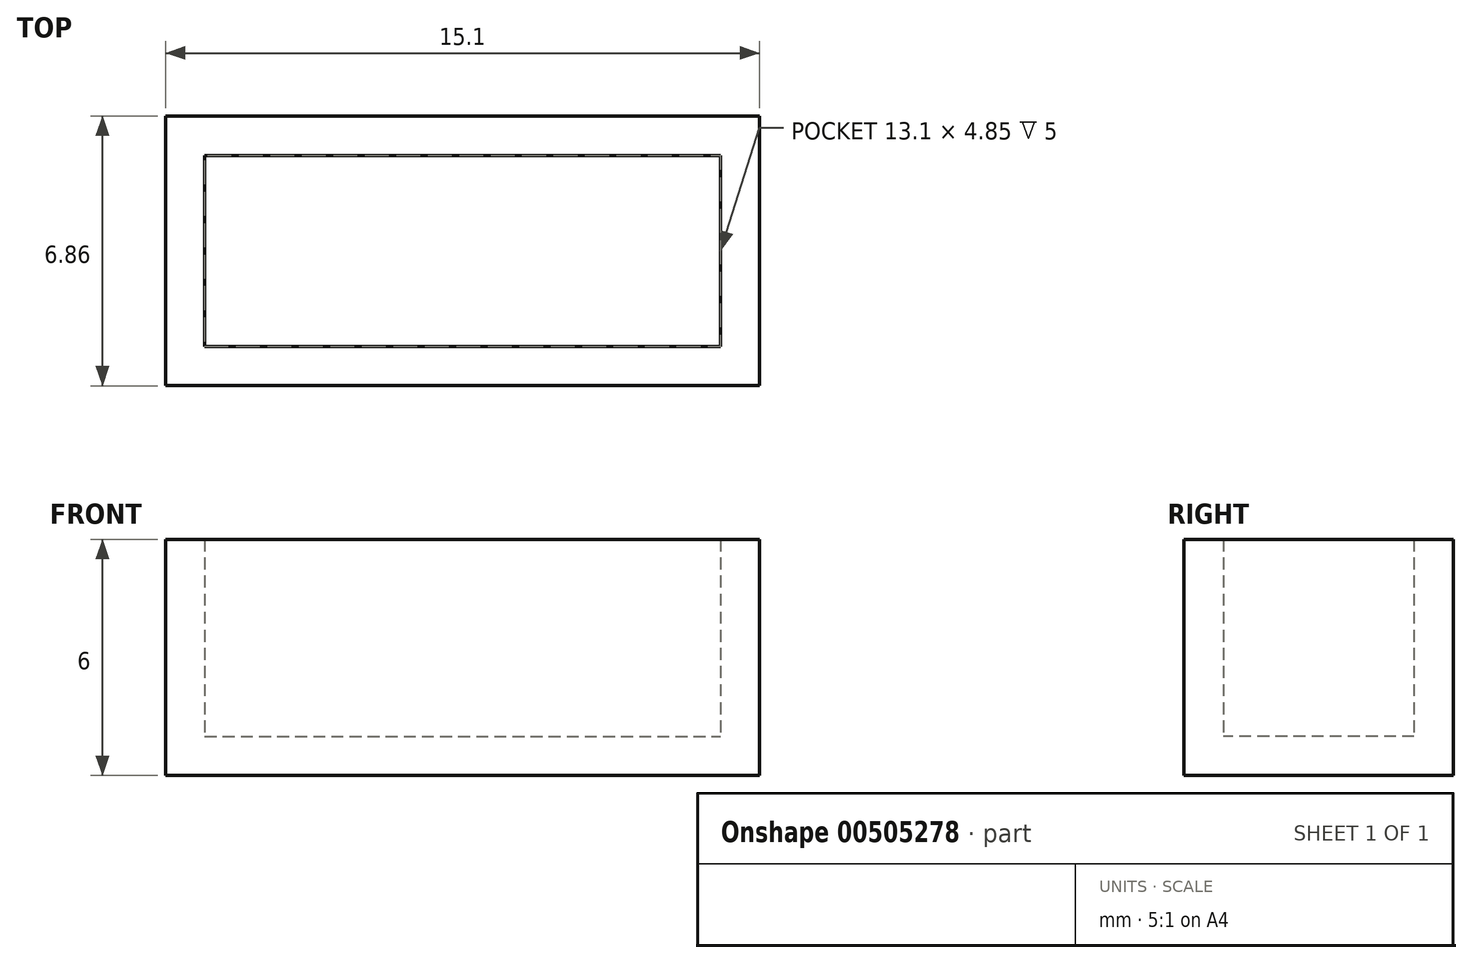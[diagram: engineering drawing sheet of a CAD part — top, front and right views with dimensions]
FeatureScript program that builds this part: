
annotation { "Feature Type Name" : "Feature", "Feature Type Description" : "" }
export const myFeature = defineFeature(function(context is Context, id is Id, definition is map)
    precondition{}
    {
        {
            var Q0;
            Q0=qCreatedBy(makeId("Top.planeOp"),FACE);
            var sketch = newSketch(context, id + "F0", { "sketchPlane" : qUnion([Q0])});
            skPoint(sketch, "E0.middle", {"position": v(0, 0) * mm});
            skLineSegment(sketch, "E1.bottom", {"start": v(-6.55, 2.42) * mm, "end": v(6.55, 2.42) * mm});
            skLineSegment(sketch, "E1.top", {"start": v(-6.55, -2.43) * mm, "end": v(6.55, -2.43) * mm});
            skLineSegment(sketch, "E1.left", {"start": v(-6.55, 2.43) * mm, "end": v(-6.55, -2.43) * mm});
            skLineSegment(sketch, "E1.right", {"start": v(6.55, 2.42) * mm, "end": v(6.55, -2.43) * mm});
            skLineSegment(sketch, "E2.bottom", {"start": v(7.55, 3.43) * mm, "end": v(-7.55, 3.43) * mm});
            skLineSegment(sketch, "E2.top", {"start": v(7.55, -3.42) * mm, "end": v(-7.55, -3.42) * mm});
            skLineSegment(sketch, "E2.left", {"start": v(7.55, 3.43) * mm, "end": v(7.55, -3.43) * mm});
            skLineSegment(sketch, "E2.right", {"start": v(-7.55, 3.43) * mm, "end": v(-7.55, -3.43) * mm});
            skSolve(sketch);
        }
        {
            var Q0;
            Q0=makeQuery(id+"F0.imprint","IMPRINT",FACE,{"disambiguationData":[TD([[makeQuery(id+"F0.imprint","IMPRINT",EDGE,{"derivedFrom":sQuery(id+"F0.wireOp",EDGE,"E1.bottom")}),1.0]])]});
            extrude(context, id + "F1", {"entities" : qUnion([Q0]), "depth" : 5 * mm});
        }
        {
            var Q0;
            Q0=makeQuery(id+"F0.imprint","IMPRINT",FACE,{"disambiguationData":[TD([[makeQuery(id+"F0.imprint","IMPRINT",EDGE,{"derivedFrom":sQuery(id+"F0.wireOp",EDGE,"E1.bottom")}),-1.0]])]});
            var Q1;
            Q1=makeQuery(id+"F0.imprint","IMPRINT",FACE,{"disambiguationData":[TD([[makeQuery(id+"F0.imprint","IMPRINT",EDGE,{"derivedFrom":sQuery(id+"F0.wireOp",EDGE,"E1.bottom")}),1.0]])]});
            extrude(context, id + "F2", {"entities" : qUnion([Q0, Q1]), "operationType" : NewBodyOperationType.ADD, "oppositeDirection" : true, "depth" : 1 * mm});
        }
    });
